# Revit family: FTXL Boiler FTX400-1000
name_source: partatom
category: Mechanical Equipment
units: mm (PartAtom-declared; Revit-internal decimal feet)

## family parameters
Always vertical = Yes
Cut with Voids When Loaded = No
OmniClass Number = 23.65.35.11.17
OmniClass Title = Thermodynamic Water Heaters
Part Type = Normal
Room Calculation Point = No
Round Connector Dimension = Use Radius
Shared = No
Work Plane-Based = No

## types (6) — shared parameters
# of Electrical Connections = 1
Clearance Visibility = Yes
Description = FTXL Fire Tube Boiler
Elec Offset from Right = 20"
FUEL TYPE = NATURAL GAS
Front Clearance = 30"
Fuel Type = Natural or LP
Manufacturer = Lochinvar
N_Water Outlet Height = 40"
O_Vent Connection Height = 12 1/2"
Rear Clearance = 24"
SES BIM Studio # = 24 0649 01
Top Clearance = 24"
URL = https://www.lochinvar.com
Voltage/Control = 24
Voltage/Heater = 120
WIDTH = 26 1/4"

## per-type parameters (varying)
- FTX1000: AIR INLET SIZE=6"; Air Inlet Radius=3"; C_Total Depth=38 1/4"; DEPTH=26 1/4"; D_Depth to Flue Centerline=34"; E_Vent Offset=10 3/4"; Elec Offset from Bottom=57"; FLA=7; F_Water Inlet Height=11"; GALLON CAPACITY=19; GAS SIZE=1 1/4"; G_Gas Conn Height=40 1/4"; Gas Radius=5/8"; HEIGHT=61 1/4"; H_Air Inlet Height=50 1/2"; INPUT RATE (BTUH)=999,000; J_Air Inlet Offset=6 3/4"; K_Offset to Gas=2 1/2"; L_Drain Height=2 1/2"; M_Water Outlet Offset=2 1/2"; P_Water Inlet Offset=7 1/2"; VENT SIZE=6"; Vent Base Radius=4 1/4"; Vent Radius=3"; WATER INLET SIZE=2 1/2"; WATER OUTLET SIZE=2 1/2"; Water Inlet Radius=1 1/4"; Water Outlet Radius=1 1/4"
- FTX850: AIR INLET SIZE=4"; Air Inlet Radius=2"; C_Total Depth=33 1/4"; DEPTH=23 1/2"; D_Depth to Flue Centerline=29"; E_Vent Offset=10"; Elec Offset from Bottom=49"; FLA=8; F_Water Inlet Height=11"; GALLON CAPACITY=16; GAS SIZE=1"; G_Gas Conn Height=40 3/4"; Gas Radius=1/2"; HEIGHT=53 1/4"; H_Air Inlet Height=48 1/4"; INPUT RATE (BTUH)=850,000; J_Air Inlet Offset=3"; K_Offset to Gas=3 1/2"; L_Drain Height=2 1/4"; M_Water Outlet Offset=2 1/4"; P_Water Inlet Offset=9"; VENT SIZE=6"; Vent Base Radius=4 1/4"; Vent Radius=3"; WATER INLET SIZE=2 1/2"; WATER OUTLET SIZE=2 1/2"; Water Inlet Radius=1 1/4"; Water Outlet Radius=1 1/4"
- FTX725: AIR INLET SIZE=4"; Air Inlet Radius=2"; C_Total Depth=33 1/4"; DEPTH=23 1/2"; D_Depth to Flue Centerline=29"; E_Vent Offset=10"; Elec Offset from Bottom=49"; FLA=6; F_Water Inlet Height=11"; GALLON CAPACITY=17; GAS SIZE=1"; G_Gas Conn Height=40 3/4"; Gas Radius=1/2"; HEIGHT=53 1/4"; H_Air Inlet Height=48 1/4"; INPUT RATE (BTUH)=725,000; J_Air Inlet Offset=3"; K_Offset to Gas=3 1/2"; L_Drain Height=2 1/4"; M_Water Outlet Offset=2 1/4"; P_Water Inlet Offset=9"; VENT SIZE=6"; Vent Base Radius=4 1/4"; Vent Radius=3"; WATER INLET SIZE=2 1/2"; WATER OUTLET SIZE=2 1/2"; Water Inlet Radius=1 1/4"; Water Outlet Radius=1 1/4"
- FTX600: AIR INLET SIZE=4"; Air Inlet Radius=2"; C_Total Depth=31"; DEPTH=23 1/2"; D_Depth to Flue Centerline=28"; E_Vent Offset=9 3/4"; Elec Offset from Bottom=49"; FLA=7; F_Water Inlet Height=10 3/4"; GALLON CAPACITY=12; GAS SIZE=1"; G_Gas Conn Height=40 3/4"; Gas Radius=1/2"; HEIGHT=53 1/4"; H_Air Inlet Height=48 1/4"; INPUT RATE (BTUH)=600,000; J_Air Inlet Offset=3 1/4"; K_Offset to Gas=3 3/4"; L_Drain Height=2 1/4"; M_Water Outlet Offset=2 1/4"; P_Water Inlet Offset=9 1/2"; VENT SIZE=4"; Vent Base Radius=3"; Vent Radius=2"; WATER INLET SIZE=2"; WATER OUTLET SIZE=2"; Water Inlet Radius=1"; Water Outlet Radius=1"
- FTX500: AIR INLET SIZE=4"; Air Inlet Radius=2"; C_Total Depth=31"; DEPTH=23 1/2"; D_Depth to Flue Centerline=28"; E_Vent Offset=9 3/4"; Elec Offset from Bottom=49"; FLA=6; F_Water Inlet Height=10 3/4"; GALLON CAPACITY=12; GAS SIZE=1"; G_Gas Conn Height=39 3/4"; Gas Radius=1/2"; HEIGHT=53 1/4"; H_Air Inlet Height=46 1/2"; INPUT RATE (BTUH)=500,000; J_Air Inlet Offset=3 1/4"; K_Offset to Gas=2 1/4"; L_Drain Height=2 1/4"; M_Water Outlet Offset=2 1/4"; P_Water Inlet Offset=9 1/2"; VENT SIZE=4"; Vent Base Radius=3"; Vent Radius=2"; WATER INLET SIZE=2"; WATER OUTLET SIZE=2"; Water Inlet Radius=1"; Water Outlet Radius=1"
- FTX400: AIR INLET SIZE=4"; Air Inlet Radius=2"; C_Total Depth=31"; DEPTH=23 1/2"; D_Depth to Flue Centerline=28"; E_Vent Offset=9 3/4"; Elec Offset from Bottom=49"; FLA=4; F_Water Inlet Height=10 3/4"; GALLON CAPACITY=13; GAS SIZE=1"; G_Gas Conn Height=40"; Gas Radius=1/2"; HEIGHT=53 1/4"; H_Air Inlet Height=46 1/2"; INPUT RATE (BTUH)=399,000; J_Air Inlet Offset=3 1/4"; K_Offset to Gas=2 1/4"; L_Drain Height=2 1/4"; M_Water Outlet Offset=2 1/4"; P_Water Inlet Offset=9 1/2"; VENT SIZE=4"; Vent Base Radius=3"; Vent Radius=2"; WATER INLET SIZE=2"; WATER OUTLET SIZE=2"; Water Inlet Radius=1"; Water Outlet Radius=1"

note: column(s) folded — value = type name in every type: MODEL NO., Model

## geometry (parser evidence)
native form markers: Sweep x2
no freeform markers — native parametric forms only
